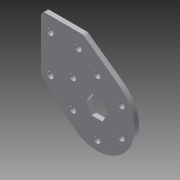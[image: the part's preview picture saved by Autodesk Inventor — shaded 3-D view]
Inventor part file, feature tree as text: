
AUTODESK INVENTOR PART (.ipt)
format: ipt  version: 2014 (Build 180170000, 170)  size: 130,560 bytes
history: native  units: in
note: dims shown in document units (in); Inventor stores cm internally (conversion verified against a paired STEP export)
features: extrude x1, fillet x1
ambient origin geometry x8: Origin, YZ Plane, XZ Plane, XY Plane, X Axis, Y Axis, Z Axis, Center Point
bodies: Solid1 (feature_tree)
feature tree (2):
  extrude  "Extrusion1"  Depth=2.0in
  fillet  "Fillet1"  Radius=0.164in
